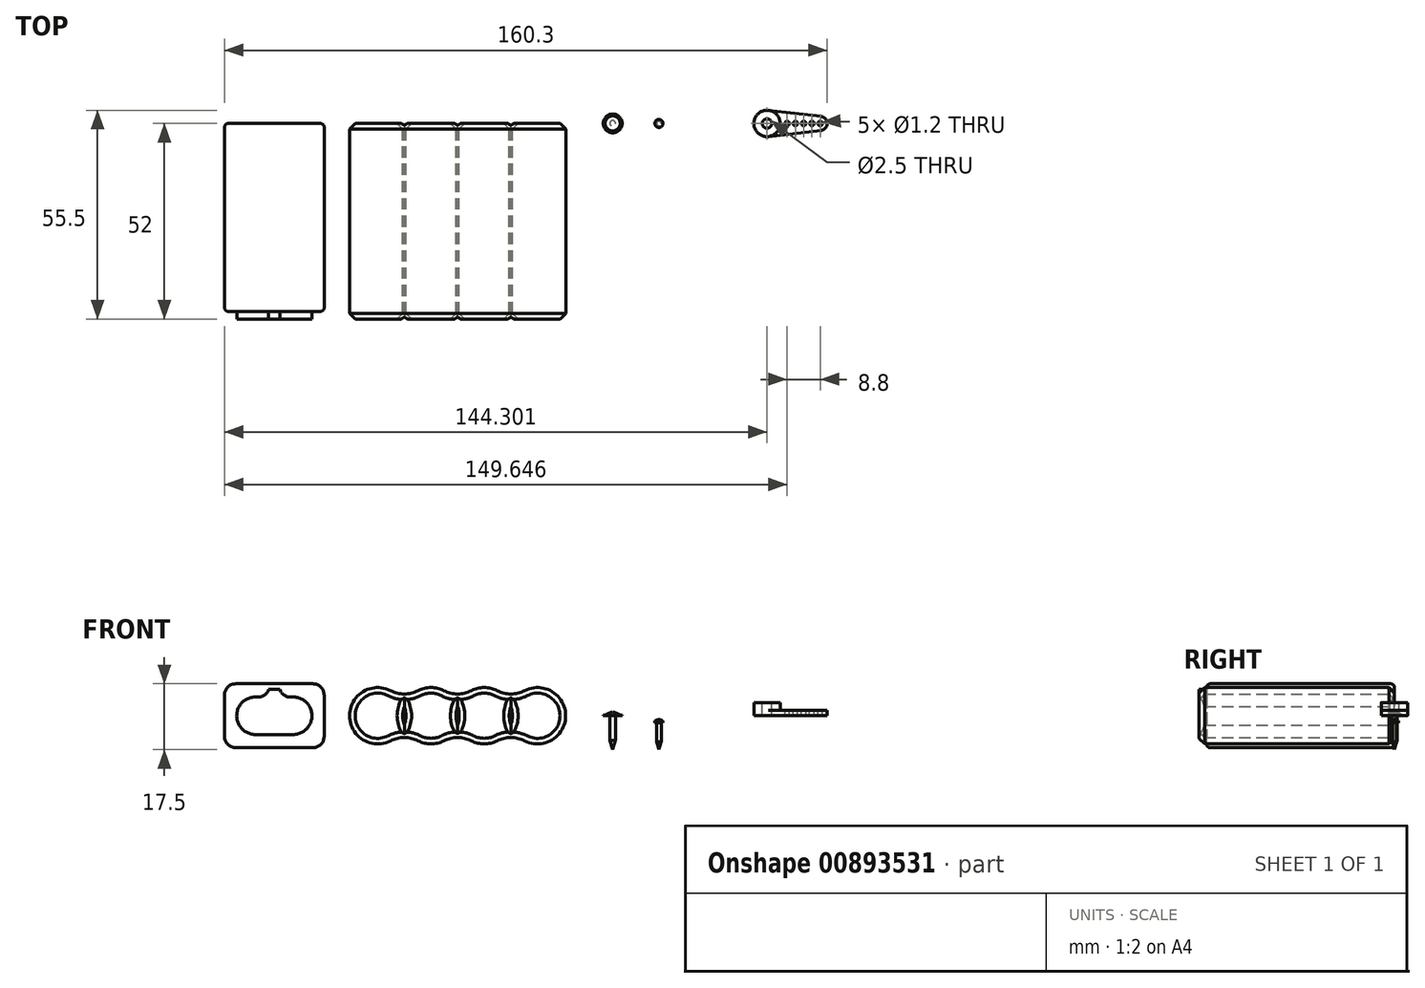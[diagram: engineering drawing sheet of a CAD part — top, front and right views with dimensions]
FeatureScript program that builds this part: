
annotation { "Feature Type Name" : "Feature", "Feature Type Description" : "" }
export const myFeature = defineFeature(function(context is Context, id is Id, definition is map)
    precondition{}
    {
        {
            var Q0;
            Q0=qCreatedBy(makeId("Front.planeOp"),FACE);
            var sketch = newSketch(context, id + "F0", { "sketchPlane" : qUnion([Q0])});
            skLineSegment(sketch, "E0", {"start": v(0, 0) * mm, "end": v(0, -9) * mm});
            skLineSegment(sketch, "E1", {"start": v(0, -9) * mm, "end": v(0.75, -6.5) * mm});
            skLineSegment(sketch, "E2", {"start": v(0.75, -6.5) * mm, "end": v(0.75, 0) * mm});
            skLineSegment(sketch, "E3", {"start": v(0.75, 0) * mm, "end": v(2.5, 0) * mm});
            skLineSegment(sketch, "E4", {"start": v(2.5, 0) * mm, "end": v(2.5, 0.2) * mm});
            skLineSegment(sketch, "E5", {"start": v(2.5, 0.2) * mm, "end": v(2, 0.2) * mm});
            skArc(sketch, "E6", {"start": v(2, 0.2) * mm, "mid": v(1.03, 0.68) * mm, "end": v(0, 1) * mm});
            skLineSegment(sketch, "E7", {"start": v(0, 1) * mm, "end": v(0, 0) * mm});
            skSolve(sketch);
        }
        {
            var Q0;
            Q0=makeQuery(id+"F0.imprint","IMPRINT",FACE,{"disambiguationData":[TD([[makeQuery(id+"F0.imprint","IMPRINT",EDGE,{"derivedFrom":sQuery(id+"F0.wireOp",EDGE,"E0")}),1.0]])]});
            var Q1;
            Q1=sQuery(id+"F0.wireOp",EDGE,"E0");
            revolve(context, id + "F1", {"surfaceOperationType" : NewSurfaceOperationType.NEW, "entities" : qUnion([Q0]), "axis" : qUnion([Q1]), "revolveType" : RevolveType.FULL});
        }
        {
            var Q0;
            Q0=makeQuery(id+"F1.opRevolve","SWEPT_BODY",BODY,{"disambiguationData":[OSD([sQuery(id+"F0.wireOp",EDGE,"E0"),sQuery(id+"F0.wireOp",EDGE,"E1"),sQuery(id+"F0.wireOp",EDGE,"E2"),sQuery(id+"F0.wireOp",EDGE,"E3"),sQuery(id+"F0.wireOp",EDGE,"E4"),sQuery(id+"F0.wireOp",EDGE,"E5"),sQuery(id+"F0.wireOp",EDGE,"E6"),sQuery(id+"F0.wireOp",EDGE,"E7")])]});
            transform(context, id + "F2", {"entities" : qUnion([Q0]), "transformType" : TransformType.TRANSLATION_3D, "dx" : 12.3 * mm, "dy" : 0 * mm, "dz" : 0 * mm, "makeCopy" : true});
        }
        {
            var Q0;
            Q0=qCreatedBy(makeId("Front.planeOp"),FACE);
            var sketch = newSketch(context, id + "F3", { "sketchPlane" : qUnion([Q0])});
            skLineSegment(sketch, "E8.bottom", {"start": v(13.64, 1.41) * mm, "end": v(15.76, 1.41) * mm});
            skLineSegment(sketch, "E8.top", {"start": v(13.64, -1.04) * mm, "end": v(15.76, -1.04) * mm});
            skLineSegment(sketch, "E8.left", {"start": v(13.64, 1.41) * mm, "end": v(13.64, -1.04) * mm});
            skLineSegment(sketch, "E8.right", {"start": v(15.76, 1.41) * mm, "end": v(15.76, -1.04) * mm});
            skLineSegment(sketch, "E9", {"start": v(12.3, 2.3) * mm, "end": v(12.3, -9) * mm});
            skSolve(sketch);
        }
        {
            var Q0;
            Q0 = qSketchRegion(id + "F3", true);
            var Q1;
            Q1=sQuery(id+"F3.wireOp",EDGE,"E9");
            revolve(context, id + "F4", {"operationType" : NewBodyOperationType.REMOVE, "surfaceOperationType" : NewSurfaceOperationType.NEW, "entities" : qUnion([Q0]), "axis" : qUnion([Q1]), "revolveType" : RevolveType.FULL, "oppositeDirection" : true});
        }
        {
            var Q0;
            Q0=makeQuery(id+"F2.opPattern","COPY",BODY,{"derivedFrom":makeQuery(id+"F1.opRevolve","SWEPT_BODY",BODY,{"disambiguationData":[OSD([sQuery(id+"F0.wireOp",EDGE,"E0"),sQuery(id+"F0.wireOp",EDGE,"E1"),sQuery(id+"F0.wireOp",EDGE,"E2"),sQuery(id+"F0.wireOp",EDGE,"E3"),sQuery(id+"F0.wireOp",EDGE,"E4"),sQuery(id+"F0.wireOp",EDGE,"E5"),sQuery(id+"F0.wireOp",EDGE,"E6"),sQuery(id+"F0.wireOp",EDGE,"E7")])]}),"instanceName":"1"});
            var Q1;
            Q1=makeQuery(id+"F2.opPattern","COPY",VERTEX,{"derivedFrom":makeQuery(id+"F1.opRevolve","SWEPT_VERTEX",VERTEX,{"disambiguationData":[OSD([sQuery(id+"F0.wireOp",EDGE,"E0"),sQuery(id+"F0.wireOp",EDGE,"E1")])]}),"instanceName":"1"});
            transform(context, id + "F5", {"entities" : qUnion([Q0]), "transformType" : TransformType.SCALE_UNIFORMLY, "scale" : 0.8, "scalePoint" : qUnion([Q1]), "makeCopy" : false});
        }
        {
            var Q0;
            Q0=qCreatedBy(makeId("Top.planeOp"),FACE);
            var sketch = newSketch(context, id + "F6", { "sketchPlane" : qUnion([Q0])});
            skCircle(sketch, "E10", {"center": v(41.05, 0) * mm, "radius": 3.5 * mm});
            skCircle(sketch, "E11", {"center": v(55.15, 0) * mm, "radius": 1.9 * mm});
            skLineSegment(sketch, "E12", {"start": v(55.37, 1.89) * mm, "end": v(41.45, 3.48) * mm});
            skLineSegment(sketch, "E13", {"start": v(55.37, -1.89) * mm, "end": v(41.45, -3.48) * mm});
            skLineSegment(sketch, "E14", {"start": v(41.05, 0) * mm, "end": v(55.15, 0) * mm, "construction": true});
            skSolve(sketch);
        }
        {
            var Q0;
            Q0 = qSketchRegion(id + "F6", true);
            extrude(context, id + "F7", {"entities" : qUnion([Q0]), "depth" : 1.5 * mm, "offsetDistance" : 25 * mm});
        }
        {
            var Q0;
            Q0=makeQuery(id+"F7.opExtrude","CAP_FACE",FACE,{"disambiguationData":[OSD([sQuery(id+"F6.wireOp",EDGE,"E10"),sQuery(id+"F6.wireOp",EDGE,"E11"),sQuery(id+"F6.wireOp",EDGE,"E12"),sQuery(id+"F6.wireOp",EDGE,"E13")])],"isStart":false});
            var sketch = newSketch(context, id + "F8", { "sketchPlane" : qUnion([Q0])});
            skCircle(sketch, "E15", {"center": v(41.05, 0) * mm, "radius": 3.5 * mm});
            skSolve(sketch);
        }
        {
            var Q0;
            Q0 = qSketchRegion(id + "F8", true);
            extrude(context, id + "F9", {"entities" : qUnion([Q0]), "operationType" : NewBodyOperationType.ADD, "depth" : 2 * mm, "offsetDistance" : 25 * mm});
        }
        {
            var Q0;
            Q0=makeQuery(id+"F9.opExtrude","CAP_FACE",FACE,{"disambiguationData":[OSD([sQuery(id+"F8.wireOp",EDGE,"E15")])],"isStart":false});
            var sketch = newSketch(context, id + "F10", { "sketchPlane" : qUnion([Q0])});
            skCircle(sketch, "E16", {"center": v(41.05, 0) * mm, "radius": 1.25 * mm});
            skSolve(sketch);
        }
        {
            var Q0;
            Q0 = qSketchRegion(id + "F10", true);
            extrude(context, id + "F11", {"entities" : qUnion([Q0]), "operationType" : NewBodyOperationType.REMOVE, "oppositeDirection" : true, "depth" : 25 * mm, "offsetDistance" : 25 * mm});
        }
        {
            var Q0;
            Q0=qCreatedBy(makeId("Front.planeOp"),FACE);
            var sketch = newSketch(context, id + "F12", { "sketchPlane" : qUnion([Q0])});
            skCircle(sketch, "E17", {"center": v(-62.5, 0) * mm, "radius": 7.5 * mm});
            skCircle(sketch, "E18", {"center": v(-48.33, 0) * mm, "radius": 7.5 * mm});
            skCircle(sketch, "E19", {"center": v(-34.17, 0) * mm, "radius": 7.5 * mm});
            skCircle(sketch, "E20", {"center": v(-20, 0) * mm, "radius": 7.5 * mm});
            skLineSegment(sketch, "E21", {"start": v(-62.5, 0) * mm, "end": v(-48.33, 0) * mm, "construction": true});
            skLineSegment(sketch, "E22", {"start": v(-48.33, 0) * mm, "end": v(-34.17, 0) * mm, "construction": true});
            skLineSegment(sketch, "E23", {"start": v(-34.17, 0) * mm, "end": v(-20, 0) * mm, "construction": true});
            skArc(sketch, "E24", {"start": v(-59.07, 6.67) * mm, "mid": v(-55.42, 5.79) * mm, "end": v(-51.76, 6.67) * mm});
            skArc(sketch, "E25", {"start": v(-44.9, 6.67) * mm, "mid": v(-41.25, 5.79) * mm, "end": v(-37.6, 6.67) * mm});
            skArc(sketch, "E26", {"start": v(-30.74, 6.67) * mm, "mid": v(-27.08, 5.79) * mm, "end": v(-23.43, 6.67) * mm});
            skArc(sketch, "E27", {"start": v(-23.43, -6.67) * mm, "mid": v(-27.08, -5.79) * mm, "end": v(-30.74, -6.67) * mm});
            skArc(sketch, "E28", {"start": v(-37.6, -6.67) * mm, "mid": v(-41.25, -5.79) * mm, "end": v(-44.9, -6.67) * mm});
            skArc(sketch, "E29", {"start": v(-51.76, -6.67) * mm, "mid": v(-55.42, -5.79) * mm, "end": v(-59.07, -6.67) * mm});
            skSolve(sketch);
        }
        {
            var Q0;
            Q0 = qSketchRegion(id + "F12", true);
            var Q1;
            {var subQ0=sQuery(id+"F12.wireOp",EDGE,"E17");var subQ1=makeQuery(id+"F12.imprint","IMPRINT",VERTEX,{"derivedFrom":subQ0});Q1=makeQuery(id+"F12.imprint","IMPRINT",FACE,{"disambiguationData":[TD([[makeQuery(id+"F12.imprint","IMPRINT",EDGE,{"disambiguationData":[TD([[subQ1,1.0]])],"derivedFrom":subQ0}),1.0]])]});}
            var Q2;
            {var subQ0=sQuery(id+"F12.wireOp",EDGE,"E18");var subQ1=makeQuery(id+"F12.imprint","IMPRINT",VERTEX,{"derivedFrom":subQ0});Q2=makeQuery(id+"F12.imprint","IMPRINT",FACE,{"disambiguationData":[TD([[makeQuery(id+"F12.imprint","IMPRINT",EDGE,{"disambiguationData":[TD([[subQ1,1.0]])],"derivedFrom":subQ0}),1.0]])]});}
            var Q3;
            {var subQ0=sQuery(id+"F12.wireOp",EDGE,"E19");var subQ1=makeQuery(id+"F12.imprint","IMPRINT",VERTEX,{"derivedFrom":subQ0});Q3=makeQuery(id+"F12.imprint","IMPRINT",FACE,{"disambiguationData":[TD([[makeQuery(id+"F12.imprint","IMPRINT",EDGE,{"disambiguationData":[TD([[subQ1,1.0]])],"derivedFrom":subQ0}),1.0]])]});}
            extrude(context, id + "F13", {"entities" : qUnion([Q0, Q1, Q2, Q3]), "depth" : 52 * mm, "offsetDistance" : 25 * mm});
        }
        {
            var Q0;
            Q0=qCreatedBy(makeId("Front.planeOp"),FACE);
            var sketch = newSketch(context, id + "F14", { "sketchPlane" : qUnion([Q0])});
            skLineSegment(sketch, "E30.bottom", {"start": v(-76.75, 8.5) * mm, "end": v(-103.25, 8.5) * mm});
            skLineSegment(sketch, "E30.top", {"start": v(-76.75, -8.5) * mm, "end": v(-103.25, -8.5) * mm});
            skLineSegment(sketch, "E30.left", {"start": v(-76.75, 8.5) * mm, "end": v(-76.75, -8.5) * mm});
            skLineSegment(sketch, "E30.right", {"start": v(-103.25, 8.5) * mm, "end": v(-103.25, -8.5) * mm});
            skPoint(sketch, "E30.middle", {"position": v(-90, 0) * mm});
            skSolve(sketch);
        }
        {
            var Q0;
            Q0 = qSketchRegion(id + "F14", true);
            extrude(context, id + "F15", {"entities" : qUnion([Q0]), "depth" : 50 * mm, "offsetDistance" : 25 * mm});
        }
        {
            var Q0;
            Q0=makeQuery(id+"F15.opExtrude","SWEPT_EDGE",EDGE,{"disambiguationData":[OSD([sQuery(id+"F14.wireOp",EDGE,"E30.bottom"),sQuery(id+"F14.wireOp",EDGE,"E30.right")])]});
            var Q1;
            Q1=makeQuery(id+"F15.opExtrude","SWEPT_EDGE",EDGE,{"disambiguationData":[OSD([sQuery(id+"F14.wireOp",EDGE,"E30.bottom"),sQuery(id+"F14.wireOp",EDGE,"E30.left")])]});
            var Q2;
            Q2=makeQuery(id+"F15.opExtrude","SWEPT_EDGE",EDGE,{"disambiguationData":[OSD([sQuery(id+"F14.wireOp",EDGE,"E30.top"),sQuery(id+"F14.wireOp",EDGE,"E30.right")])]});
            var Q3;
            Q3=makeQuery(id+"F15.opExtrude","SWEPT_EDGE",EDGE,{"disambiguationData":[OSD([sQuery(id+"F14.wireOp",EDGE,"E30.top"),sQuery(id+"F14.wireOp",EDGE,"E30.left")])]});
            fillet(context, id + "F16", {"entities" : qUnion([Q0, Q1, Q2, Q3]), "tangentPropagation" : true, "radius" : 3 * mm, "defaultsChanged" : true, "vertexSettings" : [], "allowEdgeOverflow" : false});
        }
        {
            var Q0;
            Q0=makeQuery(id+"F15.opExtrude","CAP_FACE",FACE,{"disambiguationData":[OSD([sQuery(id+"F14.wireOp",EDGE,"E30.bottom"),sQuery(id+"F14.wireOp",EDGE,"E30.top"),sQuery(id+"F14.wireOp",EDGE,"E30.left"),sQuery(id+"F14.wireOp",EDGE,"E30.right")])],"isStart":false});
            var Q1;
            Q1=makeQuery(id+"F15.opExtrude","CAP_FACE",FACE,{"disambiguationData":[OSD([sQuery(id+"F14.wireOp",EDGE,"E30.bottom"),sQuery(id+"F14.wireOp",EDGE,"E30.top"),sQuery(id+"F14.wireOp",EDGE,"E30.left"),sQuery(id+"F14.wireOp",EDGE,"E30.right")])],"isStart":true});
            fillet(context, id + "F17", {"entities" : qUnion([Q0, Q1]), "tangentPropagation" : true, "radius" : 1 * mm, "defaultsChanged" : true, "vertexSettings" : [], "allowEdgeOverflow" : false});
        }
        {
            var Q0;
            Q0=makeQuery(id+"F13.opExtrude","CAP_FACE",FACE,{"disambiguationData":[OSD([sQuery(id+"F12.wireOp",EDGE,"E17"),sQuery(id+"F12.wireOp",EDGE,"E18"),sQuery(id+"F12.wireOp",EDGE,"E19"),sQuery(id+"F12.wireOp",EDGE,"E20"),sQuery(id+"F12.wireOp",EDGE,"E24"),sQuery(id+"F12.wireOp",EDGE,"E25"),sQuery(id+"F12.wireOp",EDGE,"E26"),sQuery(id+"F12.wireOp",EDGE,"E27"),sQuery(id+"F12.wireOp",EDGE,"E28"),sQuery(id+"F12.wireOp",EDGE,"E29")])],"isStart":true});
            var Q1;
            Q1=makeQuery(id+"F13.opExtrude","CAP_FACE",FACE,{"disambiguationData":[OSD([sQuery(id+"F12.wireOp",EDGE,"E17"),sQuery(id+"F12.wireOp",EDGE,"E18"),sQuery(id+"F12.wireOp",EDGE,"E19"),sQuery(id+"F12.wireOp",EDGE,"E20"),sQuery(id+"F12.wireOp",EDGE,"E24"),sQuery(id+"F12.wireOp",EDGE,"E25"),sQuery(id+"F12.wireOp",EDGE,"E26"),sQuery(id+"F12.wireOp",EDGE,"E27"),sQuery(id+"F12.wireOp",EDGE,"E28"),sQuery(id+"F12.wireOp",EDGE,"E29")])],"isStart":false});
            chamfer(context, id + "F18", {"entities" : qUnion([Q0, Q1]), "width" : 1.5 * mm, "tangentPropagation" : true});
        }
        {
            var Q0;
            Q0=makeQuery(id+"F15.opExtrude","CAP_FACE",FACE,{"disambiguationData":[OSD([sQuery(id+"F14.wireOp",EDGE,"E30.bottom"),sQuery(id+"F14.wireOp",EDGE,"E30.top"),sQuery(id+"F14.wireOp",EDGE,"E30.left"),sQuery(id+"F14.wireOp",EDGE,"E30.right")])],"isStart":false});
            var sketch = newSketch(context, id + "F19", { "sketchPlane" : qUnion([Q0])});
            skCircle(sketch, "E31", {"center": v(-95, 0) * mm, "radius": 5 * mm});
            skCircle(sketch, "E32", {"center": v(-85, 0) * mm, "radius": 5 * mm});
            skLineSegment(sketch, "E33", {"start": v(-95, -5) * mm, "end": v(-85, -5) * mm});
            skArc(sketch, "E34", {"start": v(-88.5, 7) * mm, "mid": v(-87.37, 5.45) * mm, "end": v(-85.5, 4.97) * mm});
            skArc(sketch, "E35", {"start": v(-94.5, 4.97) * mm, "mid": v(-92.63, 5.45) * mm, "end": v(-91.5, 7) * mm});
            skLineSegment(sketch, "E36", {"start": v(-91.5, 7) * mm, "end": v(-88.5, 7) * mm});
            skLineSegment(sketch, "E37", {"start": v(-90, 7) * mm, "end": v(-90, -5) * mm, "construction": true});
            skPoint(sketch, "E37.endSnap0", {"position": v(-90, -5) * mm});
            skLineSegment(sketch, "E38", {"start": v(-90, -5) * mm, "end": v(-90, -7.5) * mm});
            skSolve(sketch);
        }
        {
            var Q0;
            Q0 = qSketchRegion(id + "F19", true);
            extrude(context, id + "F20", {"entities" : qUnion([Q0]), "depth" : 2 * mm, "offsetDistance" : 25 * mm});
        }
        {
            var Q0;
            Q0=makeQuery(id+"F7.opExtrude","CAP_FACE",FACE,{"disambiguationData":[OSD([sQuery(id+"F6.wireOp",EDGE,"E10"),sQuery(id+"F6.wireOp",EDGE,"E11"),sQuery(id+"F6.wireOp",EDGE,"E12"),sQuery(id+"F6.wireOp",EDGE,"E13")])],"isStart":false});
            var sketch = newSketch(context, id + "F21", { "sketchPlane" : qUnion([Q0])});
            skLineSegment(sketch, "E39", {"start": v(41.05, 0) * mm, "end": v(57.05, 0) * mm, "construction": true});
            skCircle(sketch, "E40", {"center": v(46.4, 0) * mm, "radius": 0.6 * mm});
            skCircle(sketch, "E41.1.0.0", {"center": v(48.6, 0) * mm, "radius": 0.6 * mm});
            skCircle(sketch, "E41.2.0.0", {"center": v(50.8, 0) * mm, "radius": 0.6 * mm});
            skCircle(sketch, "E41.3.0.0", {"center": v(53, 0) * mm, "radius": 0.6 * mm});
            skCircle(sketch, "E41.4.0.0", {"center": v(55.2, 0) * mm, "radius": 0.6 * mm});
            skLineSegment(sketch, "E41.direction1", {"start": v(46.4, 0) * mm, "end": v(48.6, 0) * mm, "construction": true});
            skSolve(sketch);
        }
        {
            var Q0;
            Q0 = qSketchRegion(id + "F21", true);
            extrude(context, id + "F22", {"entities" : qUnion([Q0]), "operationType" : NewBodyOperationType.REMOVE, "surfaceOperationType" : NewSurfaceOperationType.ADD, "oppositeDirection" : true, "depth" : 25 * mm, "offsetDistance" : 25 * mm});
        }
    });
